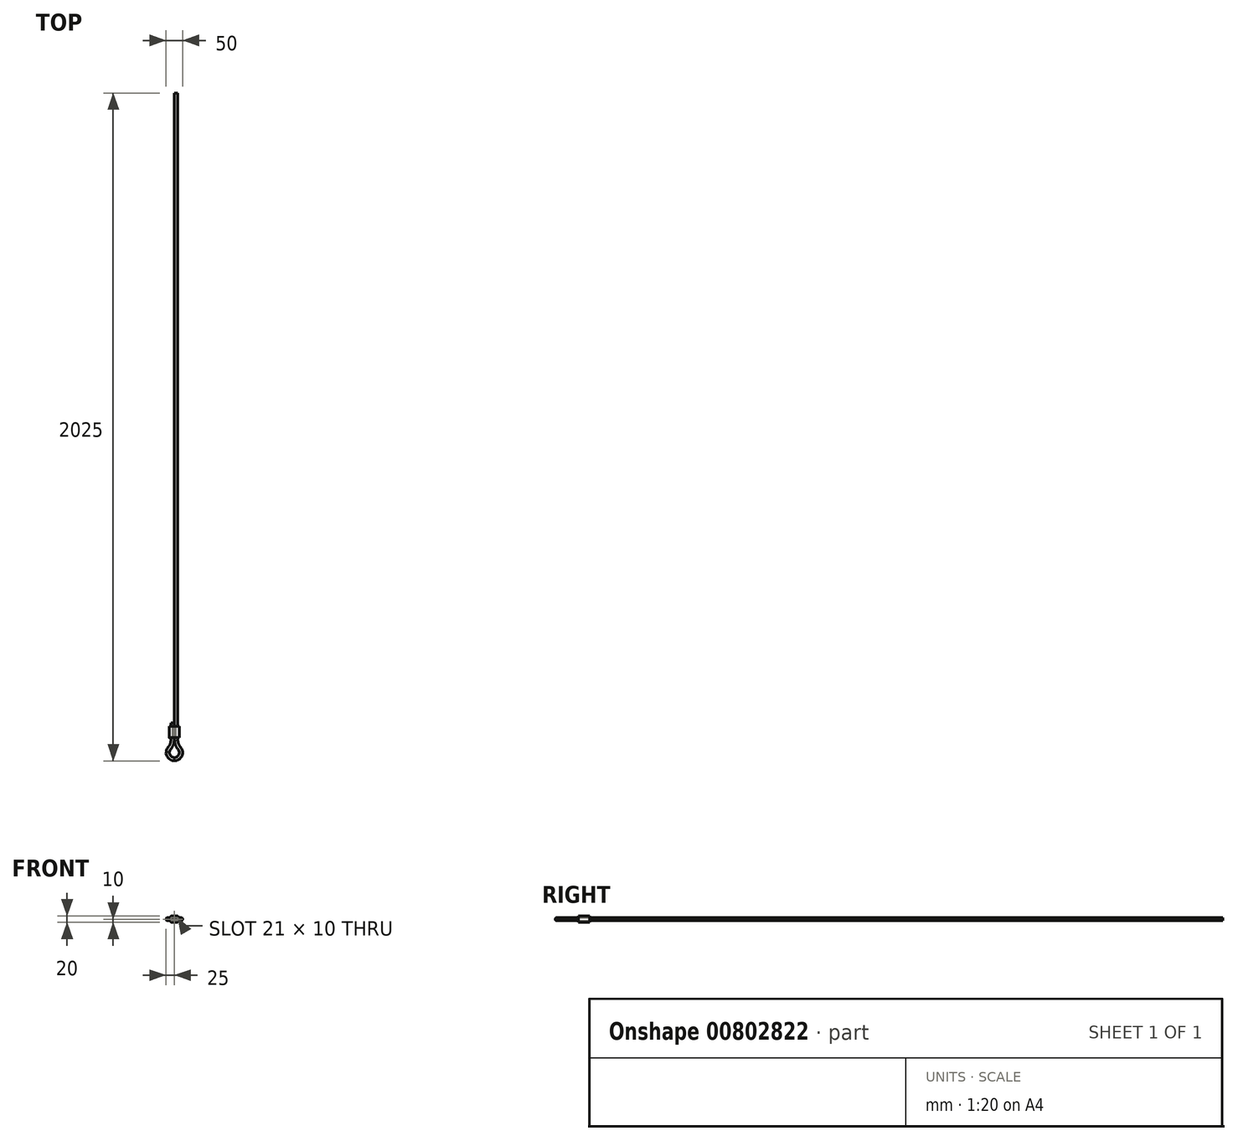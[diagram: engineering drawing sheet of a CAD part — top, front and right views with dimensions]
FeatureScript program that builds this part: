
annotation { "Feature Type Name" : "Feature", "Feature Type Description" : "" }
export const myFeature = defineFeature(function(context is Context, id is Id, definition is map)
    precondition{}
    {
        {
            var Q0;
            Q0=qCreatedBy(makeId("Top.planeOp"),FACE);
            var sketch = newSketch(context, id + "F0", { "sketchPlane" : qUnion([Q0])});
            skLineSegment(sketch, "E0", {"start": v(-5.5, 39.11) * mm, "end": v(-5.5, 90) * mm});
            skArc(sketch, "E1", {"start": v(-15.17, 13.04) * mm, "mid": v(0, -20) * mm, "end": v(15.17, 13.04) * mm});
            skArc(sketch, "E2.filletArc", {"start": v(5.5, 39.11) * mm, "mid": v(8, 25.2) * mm, "end": v(15.17, 13.04) * mm});
            skArc(sketch, "E3.filletArc", {"start": v(-15.17, 13.04) * mm, "mid": v(-8, 25.2) * mm, "end": v(-5.5, 39.11) * mm});
            skLineSegment(sketch, "E4", {"start": v(5.5, 39.11) * mm, "end": v(5.5, 2000) * mm});
            skSolve(sketch);
        }
        {
            var Q0;
            Q0=qCreatedBy(makeId("Front.planeOp"),FACE);
            var Q1;
            Q1=sQuery(id+"F0.wireOp",VERTEX,"E0.end");
            cPlane(context, id + "F1", {"entities" : qUnion([Q0, Q1]), "cplaneType" : CPlaneType.PLANE_POINT, "offset" : 25 * mm, "width" : 150 * mm, "height" : 150 * mm});
        }
        {
            var Q0;
            Q0=qCreatedBy(id+"F1.planeOp",FACE);
            var sketch = newSketch(context, id + "F2", { "sketchPlane" : qUnion([Q0])});
            skCircle(sketch, "E5", {"center": v(-5.5, 0) * mm, "radius": 5 * mm});
            skSolve(sketch);
        }
        {
            var Q0;
            Q0=makeQuery(id+"F2.imprint","IMPRINT",FACE,{"disambiguationData":[TD([[makeQuery(id+"F2.imprint","IMPRINT",EDGE,{"derivedFrom":sQuery(id+"F2.wireOp",EDGE,"E5")}),1.0]])]});
            var Q1;
            Q1 = qConstructionFilter(qBodyType(qCreatedBy(id + "F0" ,EDGE), BodyType.WIRE), ConstructionObject.NO);
            sweep(context, id + "F3", {"profiles" : qUnion([Q0]), "path" : qUnion([Q1])});
        }
        {
            var Q0;
            Q0=qCreatedBy(id+"F1.planeOp",FACE);
            cPlane(context, id + "F4", {"entities" : qUnion([Q0]), "cplaneType" : CPlaneType.OFFSET, "offset" : 10 * mm, "width" : 150 * mm, "height" : 150 * mm});
        }
        {
            var Q0;
            Q0=qCreatedBy(id+"F4.planeOp",FACE);
            var sketch = newSketch(context, id + "F5", { "sketchPlane" : qUnion([Q0])});
            skLineSegment(sketch, "E6", {"start": v(-5.5, 5) * mm, "end": v(5.5, 5) * mm});
            skLineSegment(sketch, "E7", {"start": v(-5.5, -5) * mm, "end": v(5.5, -5) * mm});
            skArc(sketch, "E8", {"start": v(5.5, 5) * mm, "mid": v(0.5, 0) * mm, "end": v(5.5, -5) * mm, "construction": true});
            skArc(sketch, "E9", {"start": v(5.5, -5) * mm, "mid": v(10.5, 0) * mm, "end": v(5.5, 5) * mm});
            skArc(sketch, "E10", {"start": v(-5.5, -5) * mm, "mid": v(-0.5, 0) * mm, "end": v(-5.5, 5) * mm, "construction": true});
            skArc(sketch, "E11", {"start": v(-5.5, 5) * mm, "mid": v(-10.5, 0) * mm, "end": v(-5.5, -5) * mm});
            skArc(sketch, "E12.0", {"start": v(5.5, -10) * mm, "mid": v(15.5, 0) * mm, "end": v(5.5, 10) * mm});
            skLineSegment(sketch, "E12.1", {"start": v(-5.5, -10) * mm, "end": v(5.5, -10) * mm});
            skArc(sketch, "E12.2", {"start": v(-5.5, 10) * mm, "mid": v(-15.5, 0) * mm, "end": v(-5.5, -10) * mm});
            skLineSegment(sketch, "E12.3", {"start": v(-5.5, 10) * mm, "end": v(5.5, 10) * mm});
            skSolve(sketch);
        }
        {
            var Q0;
            Q0 = qSketchRegion(id + "F5", true);
            extrude(context, id + "F6", {"entities" : qUnion([Q0]), "operationType" : NewBodyOperationType.ADD, "depth" : 35 * mm, "offsetDistance" : 25 * mm});
        }
    });
